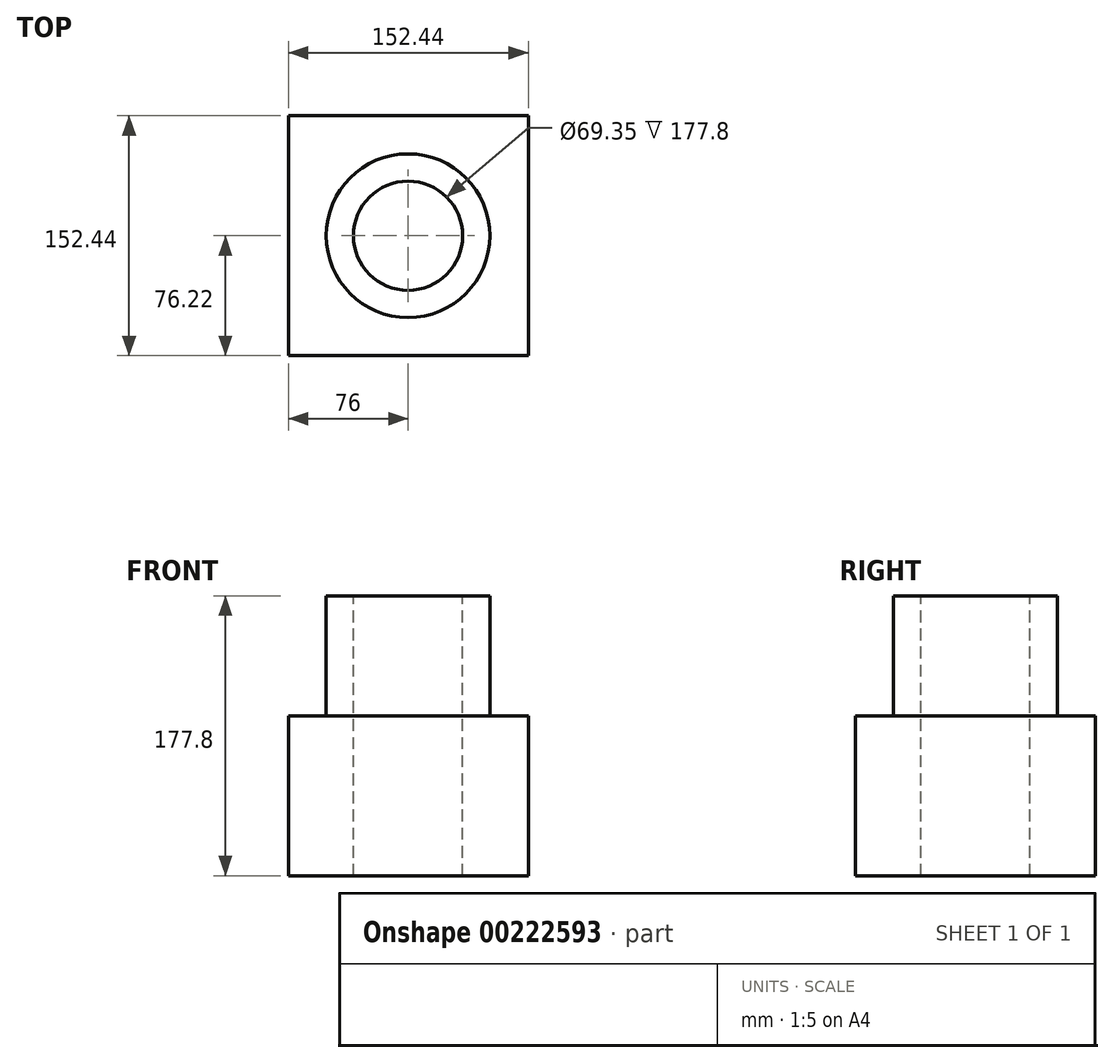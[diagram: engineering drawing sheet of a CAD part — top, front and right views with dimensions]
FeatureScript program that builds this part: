
annotation { "Feature Type Name" : "Feature", "Feature Type Description" : "" }
export const myFeature = defineFeature(function(context is Context, id is Id, definition is map)
    precondition{}
    {
        {
            var Q0;
            Q0=qCreatedBy(makeId("Top.planeOp"),FACE);
            var sketch = newSketch(context, id + "F0", { "sketchPlane" : qUnion([Q0])});
            skLineSegment(sketch, "E0.bottom", {"start": v(-76, 76.22) * mm, "end": v(76.44, 76.22) * mm});
            skLineSegment(sketch, "E0.top", {"start": v(-76, -76.22) * mm, "end": v(76.44, -76.22) * mm});
            skLineSegment(sketch, "E0.left", {"start": v(-76, 76.22) * mm, "end": v(-76, -76.22) * mm});
            skLineSegment(sketch, "E0.right", {"start": v(76.44, 76.22) * mm, "end": v(76.44, -76.22) * mm});
            skSolve(sketch);
        }
        {
            var Q0;
            Q0 = qSketchRegion(id + "F0", true);
            extrude(context, id + "F1", {"entities" : qUnion([Q0]), "depth" : 101.6 * mm});
        }
        {
            var Q0;
            Q0=makeQuery(id+"F1.opExtrude","CAP_FACE",FACE,{"disambiguationData":[OSD([sQuery(id+"F0.wireOp",EDGE,"E0.bottom"),sQuery(id+"F0.wireOp",EDGE,"E0.top"),sQuery(id+"F0.wireOp",EDGE,"E0.left"),sQuery(id+"F0.wireOp",EDGE,"E0.right")])],"isStart":false});
            var sketch = newSketch(context, id + "F2", { "sketchPlane" : qUnion([Q0])});
            skCircle(sketch, "E1", {"center": v(0, 0) * mm, "radius": 51.98 * mm});
            skSolve(sketch);
        }
        {
            var Q0;
            Q0 = qSketchRegion(id + "F2", true);
            extrude(context, id + "F3", {"entities" : qUnion([Q0]), "operationType" : NewBodyOperationType.ADD, "depth" : 76.2 * mm});
        }
        {
            var Q0;
            Q0=makeQuery(id+"F3.opExtrude","CAP_FACE",FACE,{"disambiguationData":[OSD([sQuery(id+"F2.wireOp",EDGE,"E1")])],"isStart":false});
            var sketch = newSketch(context, id + "F4", { "sketchPlane" : qUnion([Q0])});
            skCircle(sketch, "E2", {"center": v(0, 0) * mm, "radius": 34.68 * mm});
            skSolve(sketch);
        }
        {
            var Q0;
            Q0 = qSketchRegion(id + "F4", true);
            extrude(context, id + "F5", {"entities" : qUnion([Q0]), "operationType" : NewBodyOperationType.REMOVE, "endBound" : BoundingType.THROUGH_ALL, "oppositeDirection" : true, "depth" : 25.4 * mm});
        }
    });
